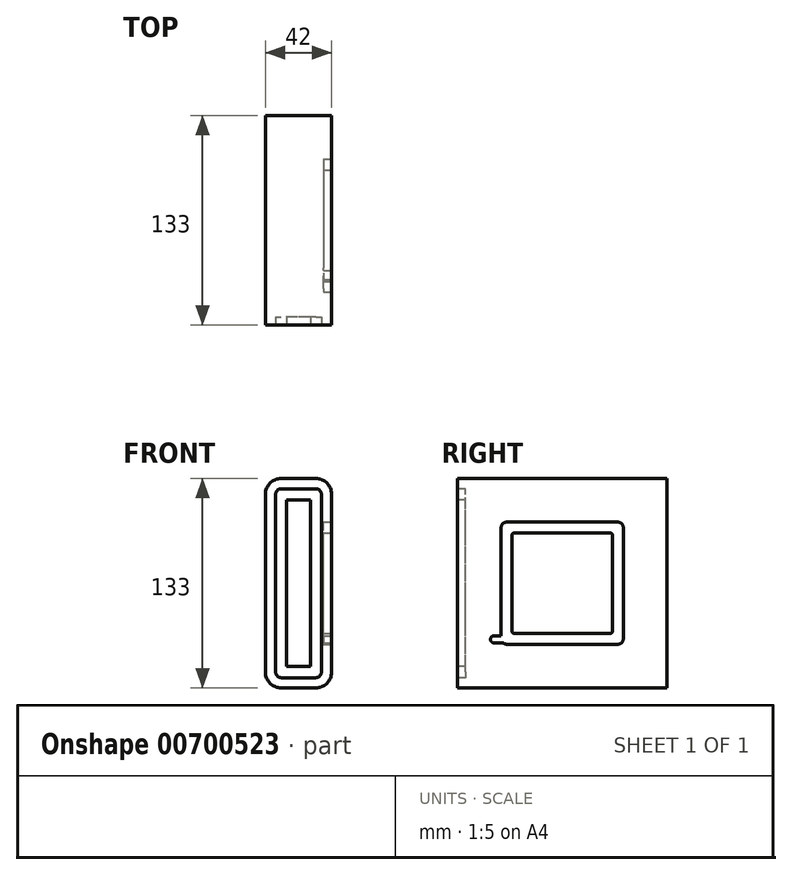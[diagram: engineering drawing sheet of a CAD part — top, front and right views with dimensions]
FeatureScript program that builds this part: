
annotation { "Feature Type Name" : "Feature", "Feature Type Description" : "" }
export const myFeature = defineFeature(function(context is Context, id is Id, definition is map)
    precondition{}
    {
        {
            var Q0;
            Q0=qCreatedBy(makeId("Top.planeOp"),FACE);
            var sketch = newSketch(context, id + "F0", { "sketchPlane" : qUnion([Q0])});
            skLineSegment(sketch, "E0.bottom", {"start": v(21, -66.5) * mm, "end": v(-21, -66.5) * mm});
            skLineSegment(sketch, "E0.top", {"start": v(21, 66.5) * mm, "end": v(-21, 66.5) * mm});
            skLineSegment(sketch, "E0.left", {"start": v(21, -66.5) * mm, "end": v(21, 66.5) * mm});
            skLineSegment(sketch, "E0.right", {"start": v(-21, -66.5) * mm, "end": v(-21, 66.5) * mm});
            skPoint(sketch, "E0.middle", {"position": v(0, 0) * mm});
            skSolve(sketch);
        }
        {
            var Q0;
            Q0 = qSketchRegion(id + "F0", true);
            extrude(context, id + "F1", {"entities" : qUnion([Q0]), "depth" : 133 * mm, "offsetDistance" : 25 * mm});
        }
        {
            var Q0;
            Q0=makeQuery(id+"F1.opExtrude","CAP_EDGE",EDGE,{"disambiguationData":[OSD([sQuery(id+"F0.wireOp",EDGE,"E0.left")])],"isStart":false});
            var Q1;
            Q1=makeQuery(id+"F1.opExtrude","CAP_EDGE",EDGE,{"disambiguationData":[OSD([sQuery(id+"F0.wireOp",EDGE,"E0.right")])],"isStart":false});
            var Q2;
            Q2=makeQuery(id+"F1.opExtrude","CAP_EDGE",EDGE,{"disambiguationData":[OSD([sQuery(id+"F0.wireOp",EDGE,"E0.left")])],"isStart":true});
            var Q3;
            Q3=makeQuery(id+"F1.opExtrude","CAP_EDGE",EDGE,{"disambiguationData":[OSD([sQuery(id+"F0.wireOp",EDGE,"E0.right")])],"isStart":true});
            fillet(context, id + "F2", {"entities" : qUnion([Q0, Q1, Q2, Q3]), "radius" : 10 * mm, "tangentPropagation" : true, "allowEdgeOverflow" : false});
        }
        {
            var Q0;
            Q0=makeQuery(id+"F1.opExtrude","SWEPT_FACE",FACE,{"disambiguationData":[OSD([sQuery(id+"F0.wireOp",EDGE,"E0.bottom")])]});
            var sketch = newSketch(context, id + "F3", { "sketchPlane" : qUnion([Q0])});
            skLineSegment(sketch, "E1.bottom", {"start": v(11, 10) * mm, "end": v(-11, 10) * mm, "construction": true});
            skLineSegment(sketch, "E1.top", {"start": v(11, 123) * mm, "end": v(-11, 123) * mm, "construction": true});
            skLineSegment(sketch, "E1.left", {"start": v(11, 10) * mm, "end": v(11, 123) * mm, "construction": true});
            skLineSegment(sketch, "E1.right", {"start": v(-11, 10) * mm, "end": v(-11, 123) * mm, "construction": true});
            skPoint(sketch, "E1.middle", {"position": v(0, 66.5) * mm});
            skArc(sketch, "E2.0.startCap", {"start": v(-7.5, 10) * mm, "mid": v(-11, 6.5) * mm, "end": v(-14.5, 10) * mm});
            skArc(sketch, "E2.0.endCap", {"start": v(-14.5, 123) * mm, "mid": v(-11, 126.5) * mm, "end": v(-7.5, 123) * mm});
            skLineSegment(sketch, "E2.0.left", {"start": v(-14.5, 10) * mm, "end": v(-14.5, 123) * mm});
            skLineSegment(sketch, "E2.0.right", {"start": v(-7.5, 10) * mm, "end": v(-7.5, 123) * mm});
            skArc(sketch, "E2.1.startCap", {"start": v(11, 126.5) * mm, "mid": v(14.5, 123) * mm, "end": v(11, 119.5) * mm});
            skArc(sketch, "E2.1.endCap", {"start": v(-11, 119.5) * mm, "mid": v(-14.5, 123) * mm, "end": v(-11, 126.5) * mm});
            skLineSegment(sketch, "E2.1.left", {"start": v(11, 119.5) * mm, "end": v(-11, 119.5) * mm});
            skLineSegment(sketch, "E2.1.right", {"start": v(11, 126.5) * mm, "end": v(-11, 126.5) * mm});
            skArc(sketch, "E2.2.startCap", {"start": v(14.5, 10) * mm, "mid": v(11, 6.5) * mm, "end": v(7.5, 10) * mm});
            skArc(sketch, "E2.2.endCap", {"start": v(7.5, 123) * mm, "mid": v(11, 126.5) * mm, "end": v(14.5, 123) * mm});
            skLineSegment(sketch, "E2.2.left", {"start": v(7.5, 10) * mm, "end": v(7.5, 123) * mm});
            skLineSegment(sketch, "E2.2.right", {"start": v(14.5, 10) * mm, "end": v(14.5, 123) * mm});
            skArc(sketch, "E2.3.startCap", {"start": v(11, 13.5) * mm, "mid": v(14.5, 10) * mm, "end": v(11, 6.5) * mm});
            skArc(sketch, "E2.3.endCap", {"start": v(-11, 6.5) * mm, "mid": v(-14.5, 10) * mm, "end": v(-11, 13.5) * mm});
            skLineSegment(sketch, "E2.3.left", {"start": v(11, 6.5) * mm, "end": v(-11, 6.5) * mm});
            skLineSegment(sketch, "E2.3.right", {"start": v(11, 13.5) * mm, "end": v(-11, 13.5) * mm});
            skSolve(sketch);
        }
        {
            var Q0;
            Q0 = qSketchRegion(id + "F3", true);
            extrude(context, id + "F4", {"entities" : qUnion([Q0]), "operationType" : NewBodyOperationType.REMOVE, "oppositeDirection" : true, "depth" : 5 * mm, "offsetDistance" : 25 * mm});
        }
        {
            var Q0;
            Q0=makeQuery(id+"F1.opExtrude","SWEPT_FACE",FACE,{"disambiguationData":[OSD([sQuery(id+"F0.wireOp",EDGE,"E0.left")])]});
            var sketch = newSketch(context, id + "F5", { "sketchPlane" : qUnion([Q0])});
            skLineSegment(sketch, "E3.bottom", {"start": v(35.38, 31.13) * mm, "end": v(-35.38, 31.12) * mm, "construction": true});
            skLineSegment(sketch, "E3.top", {"start": v(35.38, 101.88) * mm, "end": v(-35.38, 101.88) * mm, "construction": true});
            skLineSegment(sketch, "E3.left", {"start": v(35.38, 31.12) * mm, "end": v(35.38, 101.88) * mm, "construction": true});
            skLineSegment(sketch, "E3.right", {"start": v(-35.38, 31.12) * mm, "end": v(-35.38, 101.88) * mm, "construction": true});
            skPoint(sketch, "E3.middle", {"position": v(0, 66.5) * mm});
            skArc(sketch, "E4.0.startCap", {"start": v(-35.38, 27.75) * mm, "mid": v(-37.76, 28.74) * mm, "end": v(-38.75, 31.12) * mm});
            skArc(sketch, "E4.0.endCap", {"start": v(-38.75, 101.88) * mm, "mid": v(-37.76, 104.26) * mm, "end": v(-35.38, 105.25) * mm});
            skLineSegment(sketch, "E4.0.left", {"start": v(-38.75, 31.12) * mm, "end": v(-38.75, 101.88) * mm});
            skLineSegment(sketch, "E4.0.right", {"start": v(-32, 36.24) * mm, "end": v(-32, 96.76) * mm});
            skArc(sketch, "E4.1.startCap", {"start": v(35.38, 105.25) * mm, "mid": v(37.76, 104.26) * mm, "end": v(38.75, 101.88) * mm});
            skArc(sketch, "E4.1.endCap", {"start": v(-38.75, 101.88) * mm, "mid": v(-37.76, 104.26) * mm, "end": v(-35.38, 105.25) * mm});
            skLineSegment(sketch, "E4.1.left", {"start": v(30.26, 98.5) * mm, "end": v(-30.26, 98.5) * mm});
            skLineSegment(sketch, "E4.1.right", {"start": v(35.38, 105.25) * mm, "end": v(-35.38, 105.25) * mm});
            skArc(sketch, "E4.2.startCap", {"start": v(38.75, 31.13) * mm, "mid": v(37.76, 28.74) * mm, "end": v(35.38, 27.75) * mm});
            skArc(sketch, "E4.2.endCap", {"start": v(35.38, 105.25) * mm, "mid": v(37.76, 104.26) * mm, "end": v(38.75, 101.88) * mm});
            skLineSegment(sketch, "E4.2.left", {"start": v(32, 36.24) * mm, "end": v(32, 96.76) * mm});
            skLineSegment(sketch, "E4.2.right", {"start": v(38.75, 31.12) * mm, "end": v(38.75, 101.88) * mm});
            skArc(sketch, "E4.3.startCap", {"start": v(38.75, 31.12) * mm, "mid": v(37.76, 28.74) * mm, "end": v(35.38, 27.75) * mm});
            skArc(sketch, "E4.3.endCap", {"start": v(-35.38, 27.75) * mm, "mid": v(-37.76, 28.74) * mm, "end": v(-38.75, 31.12) * mm});
            skLineSegment(sketch, "E4.3.left", {"start": v(35.38, 27.75) * mm, "end": v(-35.38, 27.75) * mm});
            skLineSegment(sketch, "E4.3.right", {"start": v(30.26, 34.5) * mm, "end": v(-30.26, 34.5) * mm});
            skPoint(sketch, "E5.positionSnap0", {"position": v(-66.5, 66.5) * mm});
            skPoint(sketch, "E6.visualSharp", {"position": v(-32, 98.5) * mm});
            skArc(sketch, "E6.filletArc", {"start": v(-30.26, 98.5) * mm, "mid": v(-31.49, 97.99) * mm, "end": v(-32, 96.76) * mm});
            skPoint(sketch, "E7.visualSharp", {"position": v(32, 98.5) * mm});
            skArc(sketch, "E7.filletArc", {"start": v(32, 96.76) * mm, "mid": v(31.49, 97.99) * mm, "end": v(30.26, 98.5) * mm});
            skPoint(sketch, "E8.visualSharp", {"position": v(32, 34.5) * mm});
            skArc(sketch, "E8.filletArc", {"start": v(30.26, 34.5) * mm, "mid": v(31.49, 35.01) * mm, "end": v(32, 36.24) * mm});
            skPoint(sketch, "E9.visualSharp", {"position": v(-32, 34.5) * mm});
            skArc(sketch, "E9.filletArc", {"start": v(-32, 36.24) * mm, "mid": v(-31.49, 35.01) * mm, "end": v(-30.26, 34.5) * mm});
            skSolve(sketch);
        }
        {
            var Q0;
            Q0 = qSketchRegion(id + "F5", true);
            extrude(context, id + "F6", {"entities" : qUnion([Q0]), "operationType" : NewBodyOperationType.REMOVE, "oppositeDirection" : true, "depth" : 5 * mm, "offsetDistance" : 25 * mm});
        }
        {
            var Q0;
            {var subQ0=sQuery(id+"F0.wireOp",EDGE,"E0.left");Q0=makeQuery(id+"F6.boolean.opBoolean","SPLIT",FACE,{"disambiguationData":[TD([makeQuery(id+"F1.opExtrude","SWEPT_FACE",FACE,{"disambiguationData":[OSD([sQuery(id+"F0.wireOp",EDGE,"E0.bottom")])]})])],"derivedFrom":makeQuery(id+"F1.opExtrude","SWEPT_FACE",FACE,{"disambiguationData":[OSD([subQ0])]})});}
            var sketch = newSketch(context, id + "F7", { "sketchPlane" : qUnion([Q0])});
            skPoint(sketch, "E10", {"position": v(-38.75, 66.5) * mm});
            skPoint(sketch, "E11", {"position": v(38.75, 66.5) * mm});
            skPoint(sketch, "E12", {"position": v(0, 27.75) * mm});
            skLineSegment(sketch, "E13.0", {"start": v(30.26, 34.5) * mm, "end": v(-30.26, 34.5) * mm, "construction": true});
            skPoint(sketch, "E14", {"position": v(0, 34.5) * mm});
            skLineSegment(sketch, "E15", {"start": v(0, 34.5) * mm, "end": v(0, 27.75) * mm, "construction": true});
            skLineSegment(sketch, "E16", {"start": v(0, 30.85) * mm, "end": v(-43.33, 30.85) * mm, "construction": true});
            skArc(sketch, "E17.0.startCap", {"start": v(0, 33.1) * mm, "mid": v(2.25, 30.85) * mm, "end": v(0, 28.6) * mm});
            skArc(sketch, "E17.0.endCap", {"start": v(-43.33, 28.6) * mm, "mid": v(-45.58, 30.85) * mm, "end": v(-43.33, 33.1) * mm});
            skLineSegment(sketch, "E17.0.left", {"start": v(0, 28.6) * mm, "end": v(-43.33, 28.6) * mm});
            skLineSegment(sketch, "E17.0.right", {"start": v(0, 33.1) * mm, "end": v(-43.33, 33.1) * mm});
            skSolve(sketch);
        }
        {
            var Q0;
            Q0 = qSketchRegion(id + "F7", true);
            var Q1;
            Q1=makeQuery(id+"F6.boolean.opBoolean","COPY",FACE,{"derivedFrom":makeQuery(id+"F6.opExtrude","CAP_FACE",FACE,{"disambiguationData":[OSD([sQuery(id+"F5.wireOp",EDGE,"E4.0.left"),sQuery(id+"F5.wireOp",EDGE,"E4.0.right"),sQuery(id+"F5.wireOp",EDGE,"E4.1.endCap"),sQuery(id+"F5.wireOp",EDGE,"E4.1.left"),sQuery(id+"F5.wireOp",EDGE,"E4.1.right"),sQuery(id+"F5.wireOp",EDGE,"E4.2.endCap"),sQuery(id+"F5.wireOp",EDGE,"E4.2.left"),sQuery(id+"F5.wireOp",EDGE,"E4.2.right"),sQuery(id+"F5.wireOp",EDGE,"E4.3.startCap"),sQuery(id+"F5.wireOp",EDGE,"E4.3.endCap"),sQuery(id+"F5.wireOp",EDGE,"E4.3.left"),sQuery(id+"F5.wireOp",EDGE,"E4.3.right"),sQuery(id+"F5.wireOp",EDGE,"E6.filletArc"),sQuery(id+"F5.wireOp",EDGE,"E7.filletArc"),sQuery(id+"F5.wireOp",EDGE,"E8.filletArc"),sQuery(id+"F5.wireOp",EDGE,"E9.filletArc")])],"isStart":false})});
            extrude(context, id + "F8", {"entities" : qUnion([Q0]), "operationType" : NewBodyOperationType.REMOVE, "endBound" : BoundingType.UP_TO_SURFACE, "oppositeDirection" : true, "depth" : 25 * mm, "endBoundEntityFace" : qUnion([Q1]), "offsetDistance" : 25 * mm});
        }
        {
            var Q0;
            Q0=makeQuery(id+"F6.boolean.opBoolean","COPY",EDGE,{"derivedFrom":makeQuery(id+"F6.opExtrude","CAP_EDGE",EDGE,{"disambiguationData":[OSD([sQuery(id+"F5.wireOp",EDGE,"E4.2.left")])],"isStart":true})});
            cPoint(context, id + "F9", {"entities" : qUnion([Q0]), "parameter" : 0.5});
        }
        {
            var Q0;
            Q0 = qCreatedBy(id + "F9" ,VERTEX);
            var Q1;
            Q1=qCreatedBy(makeId("Top.planeOp"),FACE);
            cPlane(context, id + "F10", {"entities" : qUnion([Q0, Q1]), "cplaneType" : CPlaneType.PLANE_POINT, "offset" : 25 * mm, "width" : 150 * mm, "height" : 150 * mm});
        }
        {
            var Q0;
            Q0=qCreatedBy(id+"F10.planeOp",FACE);
            var sketch = newSketch(context, id + "F11", { "sketchPlane" : qUnion([Q0])});
            skLineSegment(sketch, "E18", {"start": v(0, 0) * mm, "end": v(78, 0) * mm, "construction": true});
            skSolve(sketch);
        }
    });
